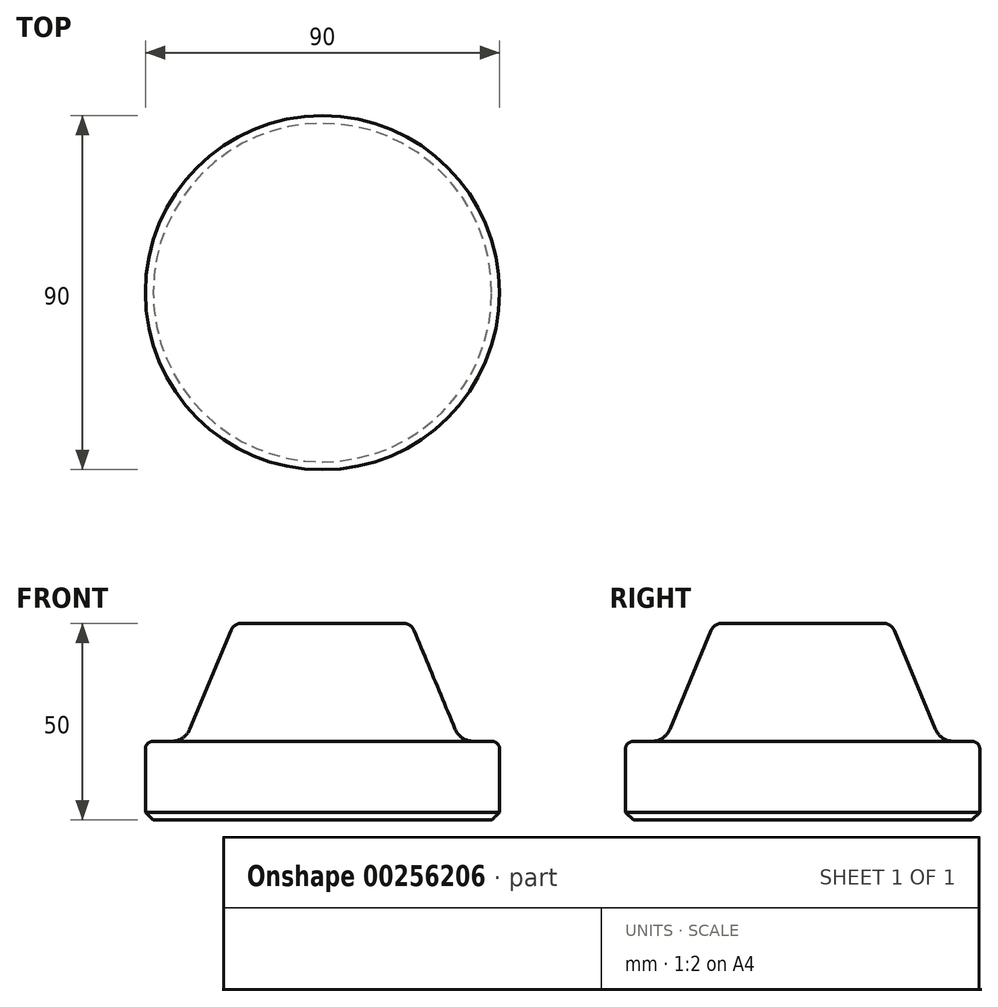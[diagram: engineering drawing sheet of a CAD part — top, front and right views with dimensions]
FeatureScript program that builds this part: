
annotation { "Feature Type Name" : "Feature", "Feature Type Description" : "" }
export const myFeature = defineFeature(function(context is Context, id is Id, definition is map)
    precondition{}
    {
        {
            var Q0;
            Q0=qCreatedBy(makeId("Front.planeOp"),FACE);
            var sketch = newSketch(context, id + "F0", { "sketchPlane" : qUnion([Q0])});
            skLineSegment(sketch, "E0", {"start": v(0, 50) * mm, "end": v(0, 0) * mm});
            skLineSegment(sketch, "E1", {"start": v(0, 0) * mm, "end": v(45, 0) * mm});
            skLineSegment(sketch, "E2", {"start": v(45, 0) * mm, "end": v(45, 18) * mm});
            skLineSegment(sketch, "E3", {"start": v(43, 20) * mm, "end": v(38.33, 20) * mm});
            skLineSegment(sketch, "E4", {"start": v(33.72, 23.08) * mm, "end": v(23.27, 48.15) * mm});
            skLineSegment(sketch, "E5", {"start": v(20.5, 50) * mm, "end": v(0, 50) * mm});
            skPoint(sketch, "E6.visualSharp", {"position": v(22.5, 50) * mm});
            skArc(sketch, "E6.filletArc", {"start": v(23.27, 48.15) * mm, "mid": v(22.16, 49.5) * mm, "end": v(20.5, 50) * mm});
            skPoint(sketch, "E7.visualSharp", {"position": v(35, 20) * mm});
            skArc(sketch, "E7.filletArc", {"start": v(33.72, 23.08) * mm, "mid": v(35.56, 20.84) * mm, "end": v(38.33, 20) * mm});
            skPoint(sketch, "E8.visualSharp", {"position": v(45, 20) * mm});
            skArc(sketch, "E8.filletArc", {"start": v(45, 18) * mm, "mid": v(44.41, 19.41) * mm, "end": v(43, 20) * mm});
            skLineSegment(sketch, "E9", {"start": v(0, 71.75) * mm, "end": v(0, -35.27) * mm, "construction": true});
            skSolve(sketch);
        }
        {
            var Q0;
            Q0=makeQuery(id+"F0.imprint","IMPRINT",FACE,{"disambiguationData":[TD([[makeQuery(id+"F0.imprint","IMPRINT",EDGE,{"derivedFrom":sQuery(id+"F0.wireOp",EDGE,"E0")}),1.0]])]});
            var Q1;
            Q1=sQuery(id+"F0.wireOp",EDGE,"E9");
            revolve(context, id + "F1", {"entities" : qUnion([Q0]), "axis" : qUnion([Q1]), "revolveType" : RevolveType.FULL});
        }
        {
            var Q0;
            Q0=makeQuery(id+"F1.opRevolve","SWEPT_EDGE",EDGE,{"disambiguationData":[OSD([sQuery(id+"F0.wireOp",EDGE,"E1"),sQuery(id+"F0.wireOp",EDGE,"E2")])]});
            chamfer(context, id + "F2", {"entities" : qUnion([Q0]), "width" : 2 * mm, "tangentPropagation" : true});
        }
    });
